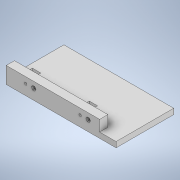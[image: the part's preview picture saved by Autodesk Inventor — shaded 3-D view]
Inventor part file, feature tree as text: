
AUTODESK INVENTOR PART (.ipt)
format: ipt  version: 2020 (Build 240168000, 168)  size: 184,320 bytes
history: native  units: mm
features: other x5, mirror x1
ambient origin geometry x8: Origin, YZ Plane, XZ Plane, XY Plane, X Axis, Y Axis, Z Axis, Center Point
bodies: Body1 (feature_tree)
feature tree (6):
  other  "side_bumper_lower_R_new.ipt"
  mirror  "미러2"
  other  "솔리드1::side_bumper_lower_R_new.ipt"
  other  "피쳐 태그2"
  other  "솔리드2"
  other  "솔리드1"
